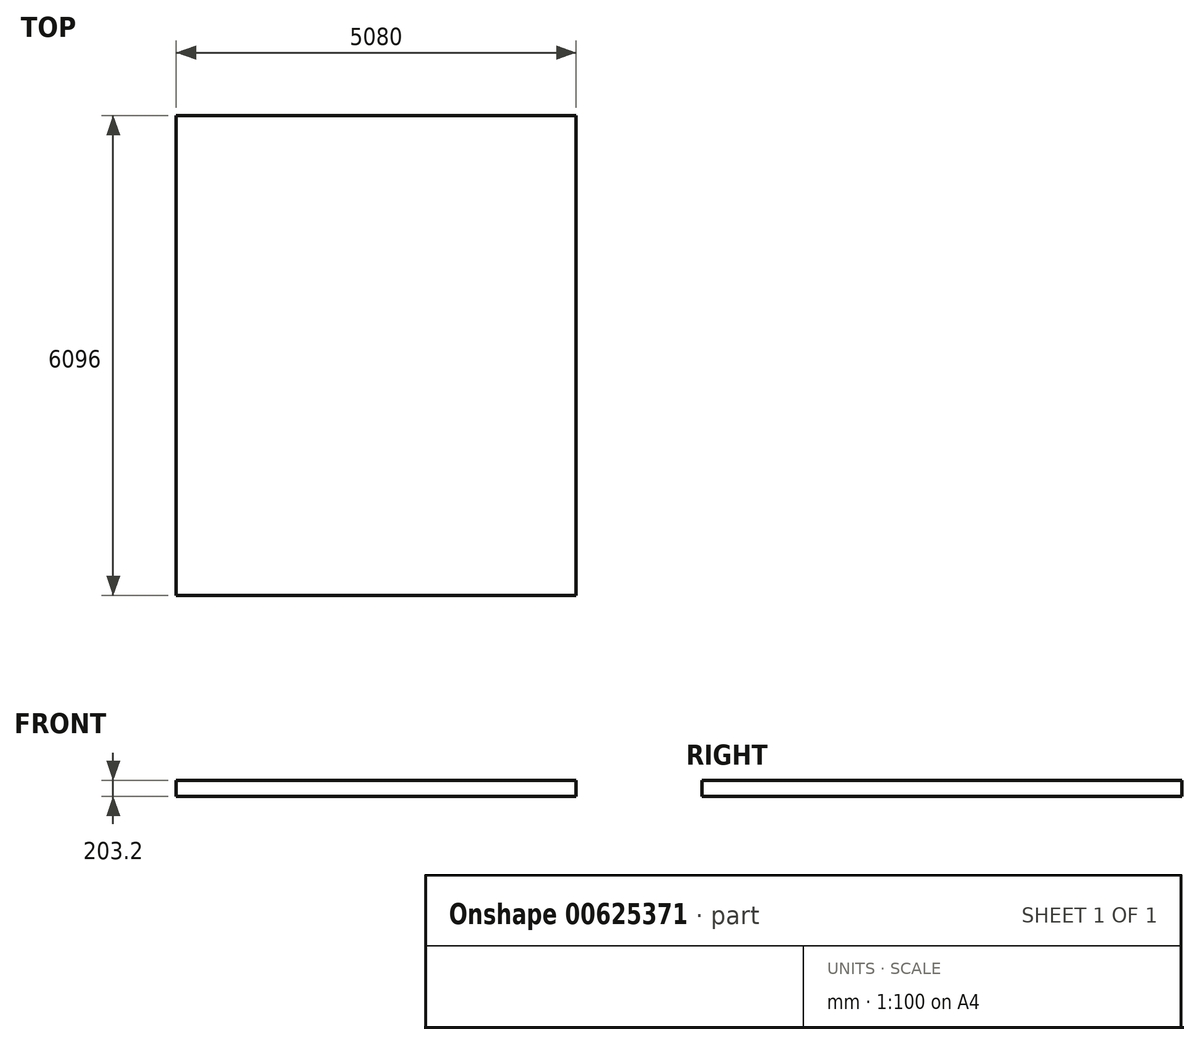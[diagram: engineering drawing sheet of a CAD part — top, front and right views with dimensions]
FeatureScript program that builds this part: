
annotation { "Feature Type Name" : "Feature", "Feature Type Description" : "" }
export const myFeature = defineFeature(function(context is Context, id is Id, definition is map)
    precondition{}
    {
        {
            var Q0;
            Q0=qCreatedBy(makeId("Front.planeOp"),FACE);
            var sketch = newSketch(context, id + "F0", { "sketchPlane" : qUnion([Q0])});
            skLineSegment(sketch, "E0.bottom", {"start": v(-76.39, 0) * mm, "end": v(5003.61, 0) * mm});
            skLineSegment(sketch, "E0.top", {"start": v(-76.39, -203.2) * mm, "end": v(5003.61, -203.2) * mm});
            skLineSegment(sketch, "E0.left", {"start": v(-76.39, 0) * mm, "end": v(-76.39, -203.2) * mm});
            skLineSegment(sketch, "E0.right", {"start": v(5003.61, 0) * mm, "end": v(5003.61, -203.2) * mm});
            skSolve(sketch);
        }
        {
            var Q0;
            Q0=makeQuery(id+"F0.imprint","IMPRINT",FACE,{"disambiguationData":[TD([[makeQuery(id+"F0.imprint","IMPRINT",EDGE,{"derivedFrom":sQuery(id+"F0.wireOp",EDGE,"E0.bottom")}),-1.0]])]});
            extrude(context, id + "F1", {"entities" : qUnion([Q0]), "depth" : 6096 * mm, "offsetDistance" : 25.4 * mm});
        }
    });
